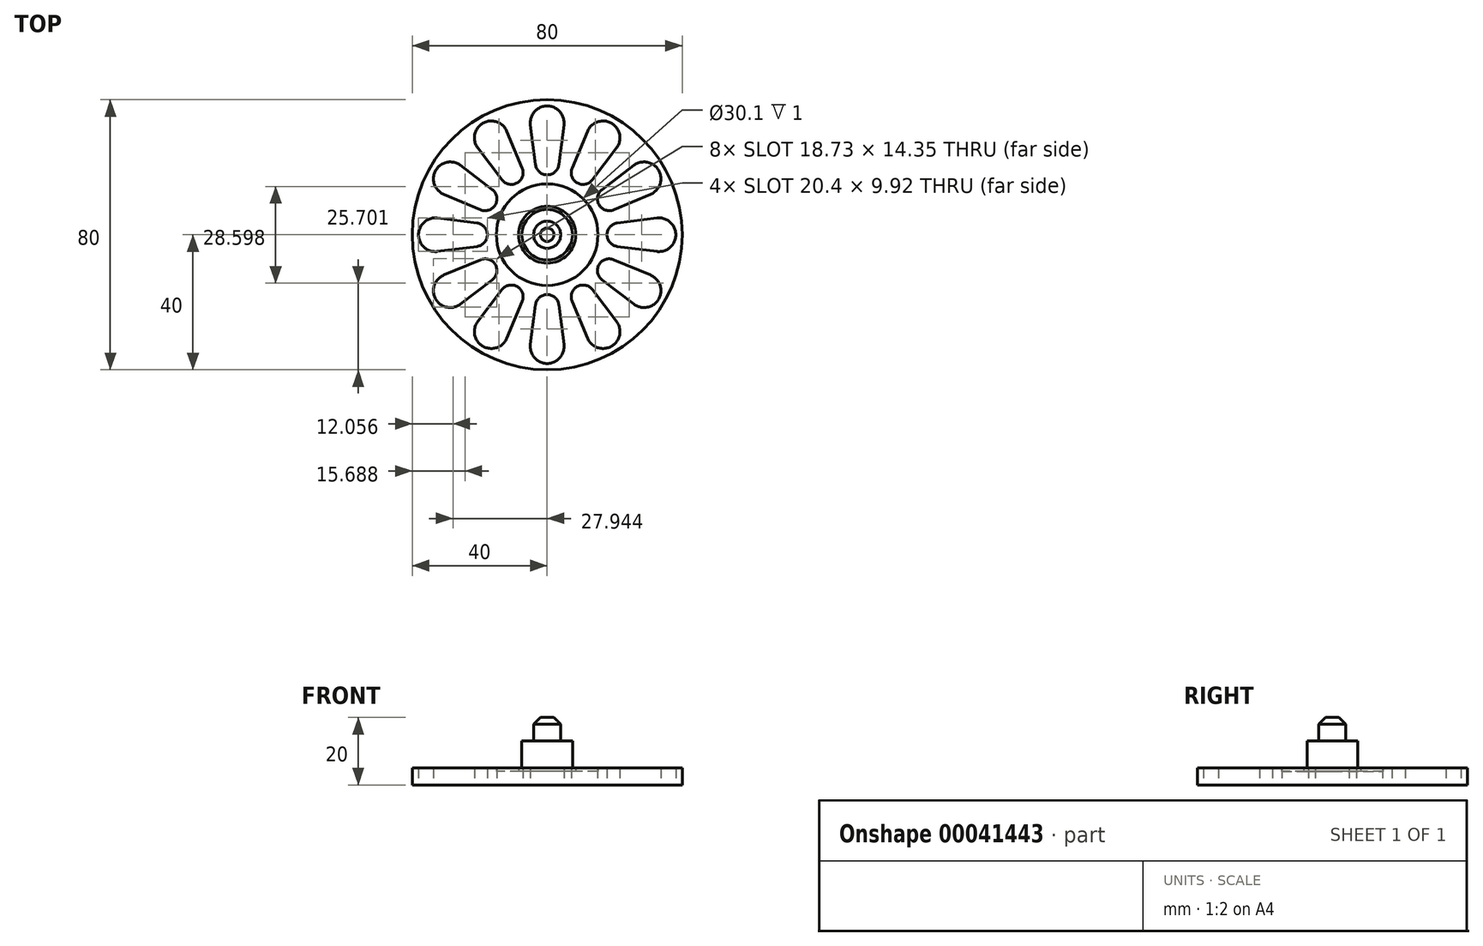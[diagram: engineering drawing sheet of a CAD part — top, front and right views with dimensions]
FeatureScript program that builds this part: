
annotation { "Feature Type Name" : "Feature", "Feature Type Description" : "" }
export const myFeature = defineFeature(function(context is Context, id is Id, definition is map)
    precondition{}
    {
        {
            var Q0;
            Q0=qCreatedBy(makeId("Top.planeOp"),FACE);
            var sketch = newSketch(context, id + "F0", { "sketchPlane" : qUnion([Q0])});
            skCircle(sketch, "E0", {"center": v(0, 0) * mm, "radius": 40 * mm});
            skCircle(sketch, "E1", {"center": v(0, 0) * mm, "radius": 8.45 * mm});
            skCircle(sketch, "E2", {"center": v(0, 0) * mm, "radius": 15.05 * mm});
            skArc(sketch, "E3", {"start": v(-3.47, 20.8) * mm, "mid": v(0, 17.74) * mm, "end": v(3.47, 20.8) * mm});
            skArc(sketch, "E4", {"start": v(4.96, 32.51) * mm, "mid": v(0, 38.14) * mm, "end": v(-4.96, 32.51) * mm});
            skLineSegment(sketch, "E5", {"start": v(-3.47, 20.8) * mm, "end": v(-4.96, 32.51) * mm});
            skLineSegment(sketch, "E6", {"start": v(4.96, 32.51) * mm, "end": v(3.47, 20.8) * mm});
            skArc(sketch, "E7.1.0", {"start": v(-11.96, 30.64) * mm, "mid": v(-19.07, 33.03) * mm, "end": v(-20.55, 25.68) * mm});
            skLineSegment(sketch, "E7.1.1", {"start": v(-13.4, 16.28) * mm, "end": v(-20.55, 25.68) * mm});
            skLineSegment(sketch, "E7.1.2", {"start": v(-11.96, 30.64) * mm, "end": v(-7.4, 19.75) * mm});
            skArc(sketch, "E7.1.3", {"start": v(-13.4, 16.28) * mm, "mid": v(-8.87, 15.37) * mm, "end": v(-7.4, 19.75) * mm});
            skArc(sketch, "E7.2.0", {"start": v(-25.68, 20.55) * mm, "mid": v(-33.03, 19.07) * mm, "end": v(-30.64, 11.96) * mm});
            skLineSegment(sketch, "E7.2.1", {"start": v(-19.75, 7.4) * mm, "end": v(-30.64, 11.96) * mm});
            skLineSegment(sketch, "E7.2.2", {"start": v(-25.68, 20.55) * mm, "end": v(-16.28, 13.4) * mm});
            skArc(sketch, "E7.2.3", {"start": v(-19.75, 7.4) * mm, "mid": v(-15.37, 8.87) * mm, "end": v(-16.28, 13.4) * mm});
            skArc(sketch, "E7.3.0", {"start": v(-32.51, 4.96) * mm, "mid": v(-38.14, 0) * mm, "end": v(-32.51, -4.96) * mm});
            skLineSegment(sketch, "E7.3.1", {"start": v(-20.8, -3.47) * mm, "end": v(-32.51, -4.96) * mm});
            skLineSegment(sketch, "E7.3.2", {"start": v(-32.51, 4.96) * mm, "end": v(-20.8, 3.47) * mm});
            skArc(sketch, "E7.3.3", {"start": v(-20.8, -3.47) * mm, "mid": v(-17.74, 0) * mm, "end": v(-20.8, 3.47) * mm});
            skArc(sketch, "E7.4.0", {"start": v(-30.64, -11.96) * mm, "mid": v(-33.03, -19.07) * mm, "end": v(-25.68, -20.55) * mm});
            skLineSegment(sketch, "E7.4.1", {"start": v(-16.28, -13.4) * mm, "end": v(-25.68, -20.55) * mm});
            skLineSegment(sketch, "E7.4.2", {"start": v(-30.64, -11.96) * mm, "end": v(-19.75, -7.4) * mm});
            skArc(sketch, "E7.4.3", {"start": v(-16.28, -13.4) * mm, "mid": v(-15.37, -8.87) * mm, "end": v(-19.75, -7.4) * mm});
            skArc(sketch, "E7.5.0", {"start": v(-20.55, -25.68) * mm, "mid": v(-19.07, -33.03) * mm, "end": v(-11.96, -30.64) * mm});
            skLineSegment(sketch, "E7.5.1", {"start": v(-7.4, -19.75) * mm, "end": v(-11.96, -30.64) * mm});
            skLineSegment(sketch, "E7.5.2", {"start": v(-20.55, -25.68) * mm, "end": v(-13.4, -16.28) * mm});
            skArc(sketch, "E7.5.3", {"start": v(-7.4, -19.75) * mm, "mid": v(-8.87, -15.37) * mm, "end": v(-13.4, -16.28) * mm});
            skArc(sketch, "E7.6.0", {"start": v(-4.96, -32.51) * mm, "mid": v(0, -38.14) * mm, "end": v(4.96, -32.51) * mm});
            skLineSegment(sketch, "E7.6.1", {"start": v(3.47, -20.8) * mm, "end": v(4.96, -32.51) * mm});
            skLineSegment(sketch, "E7.6.2", {"start": v(-4.96, -32.51) * mm, "end": v(-3.47, -20.8) * mm});
            skArc(sketch, "E7.6.3", {"start": v(3.47, -20.8) * mm, "mid": v(0, -17.74) * mm, "end": v(-3.47, -20.8) * mm});
            skArc(sketch, "E7.7.0", {"start": v(11.96, -30.64) * mm, "mid": v(19.07, -33.03) * mm, "end": v(20.55, -25.68) * mm});
            skLineSegment(sketch, "E7.7.1", {"start": v(13.4, -16.28) * mm, "end": v(20.55, -25.68) * mm});
            skLineSegment(sketch, "E7.7.2", {"start": v(11.96, -30.64) * mm, "end": v(7.4, -19.75) * mm});
            skArc(sketch, "E7.7.3", {"start": v(13.4, -16.28) * mm, "mid": v(8.87, -15.37) * mm, "end": v(7.4, -19.75) * mm});
            skArc(sketch, "E7.8.0", {"start": v(25.68, -20.55) * mm, "mid": v(33.03, -19.07) * mm, "end": v(30.64, -11.96) * mm});
            skLineSegment(sketch, "E7.8.1", {"start": v(19.75, -7.4) * mm, "end": v(30.64, -11.96) * mm});
            skLineSegment(sketch, "E7.8.2", {"start": v(25.68, -20.55) * mm, "end": v(16.28, -13.4) * mm});
            skArc(sketch, "E7.8.3", {"start": v(19.75, -7.4) * mm, "mid": v(15.37, -8.87) * mm, "end": v(16.28, -13.4) * mm});
            skArc(sketch, "E7.9.0", {"start": v(32.51, -4.96) * mm, "mid": v(38.14, 0) * mm, "end": v(32.51, 4.96) * mm});
            skLineSegment(sketch, "E7.9.1", {"start": v(20.8, 3.47) * mm, "end": v(32.51, 4.96) * mm});
            skLineSegment(sketch, "E7.9.2", {"start": v(32.51, -4.96) * mm, "end": v(20.8, -3.47) * mm});
            skArc(sketch, "E7.9.3", {"start": v(20.8, 3.47) * mm, "mid": v(17.74, 0) * mm, "end": v(20.8, -3.47) * mm});
            skArc(sketch, "E7.10.0", {"start": v(30.64, 11.96) * mm, "mid": v(33.03, 19.07) * mm, "end": v(25.68, 20.55) * mm});
            skLineSegment(sketch, "E7.10.1", {"start": v(16.28, 13.4) * mm, "end": v(25.68, 20.55) * mm});
            skLineSegment(sketch, "E7.10.2", {"start": v(30.64, 11.96) * mm, "end": v(19.75, 7.4) * mm});
            skArc(sketch, "E7.10.3", {"start": v(16.28, 13.4) * mm, "mid": v(15.37, 8.87) * mm, "end": v(19.75, 7.4) * mm});
            skArc(sketch, "E7.11.0", {"start": v(20.55, 25.68) * mm, "mid": v(19.07, 33.03) * mm, "end": v(11.96, 30.64) * mm});
            skLineSegment(sketch, "E7.11.1", {"start": v(7.4, 19.75) * mm, "end": v(11.96, 30.64) * mm});
            skLineSegment(sketch, "E7.11.2", {"start": v(20.55, 25.68) * mm, "end": v(13.4, 16.28) * mm});
            skArc(sketch, "E7.11.3", {"start": v(7.4, 19.75) * mm, "mid": v(8.87, 15.37) * mm, "end": v(13.4, 16.28) * mm});
            skCircle(sketch, "E8", {"center": v(0, 0) * mm, "radius": 7.5 * mm});
            skCircle(sketch, "E9", {"center": v(0, 0) * mm, "radius": 4 * mm});
            skSolve(sketch);
        }
        {
            var Q0;
            Q0=makeQuery(id+"F0.imprint","IMPRINT",FACE,{"disambiguationData":[TD([[makeQuery(id+"F0.imprint","IMPRINT",EDGE,{"derivedFrom":sQuery(id+"F0.wireOp",EDGE,"E0")}),1.0]])]});
            extrude(context, id + "F1", {"entities" : qUnion([Q0]), "depth" : 5 * mm});
        }
        {
            var Q0;
            Q0=makeQuery(id+"F0.imprint","IMPRINT",FACE,{"disambiguationData":[TD([[makeQuery(id+"F0.imprint","IMPRINT",EDGE,{"derivedFrom":sQuery(id+"F0.wireOp",EDGE,"E1")}),-1.0]])]});
            extrude(context, id + "F2", {"entities" : qUnion([Q0]), "operationType" : NewBodyOperationType.ADD, "depth" : 4 * mm});
        }
        {
            var Q0;
            Q0=makeQuery(id+"F0.imprint","IMPRINT",FACE,{"disambiguationData":[TD([[makeQuery(id+"F0.imprint","IMPRINT",EDGE,{"derivedFrom":sQuery(id+"F0.wireOp",EDGE,"E1")}),1.0]])]});
            extrude(context, id + "F3", {"entities" : qUnion([Q0]), "operationType" : NewBodyOperationType.ADD, "depth" : 5 * mm});
        }
        {
            var Q0;
            Q0=makeQuery(id+"F0.imprint","IMPRINT",FACE,{"disambiguationData":[TD([[makeQuery(id+"F0.imprint","IMPRINT",EDGE,{"derivedFrom":sQuery(id+"F0.wireOp",EDGE,"E8")}),1.0]])]});
            extrude(context, id + "F4", {"entities" : qUnion([Q0]), "operationType" : NewBodyOperationType.ADD, "depth" : 13 * mm});
        }
        {
            var Q0;
            Q0=makeQuery(id+"F0.imprint","IMPRINT",FACE,{"disambiguationData":[TD([[makeQuery(id+"F0.imprint","IMPRINT",EDGE,{"derivedFrom":sQuery(id+"F0.wireOp",EDGE,"E9")}),1.0]])]});
            extrude(context, id + "F5", {"entities" : qUnion([Q0]), "operationType" : NewBodyOperationType.ADD, "depth" : 20 * mm});
        }
        {
            var Q0;
            Q0=makeQuery(id+"F5.opExtrude","CAP_FACE",FACE,{"disambiguationData":[OSD([sQuery(id+"F0.wireOp",EDGE,"E9")])],"isStart":false});
            chamfer(context, id + "F6", {"entities" : qUnion([Q0]), "chamferType" : ChamferType.TWO_OFFSETS, "width1" : 2 * mm, "oppositeDirection" : false, "width2" : 2 * mm, "tangentPropagation" : true});
        }
    });
